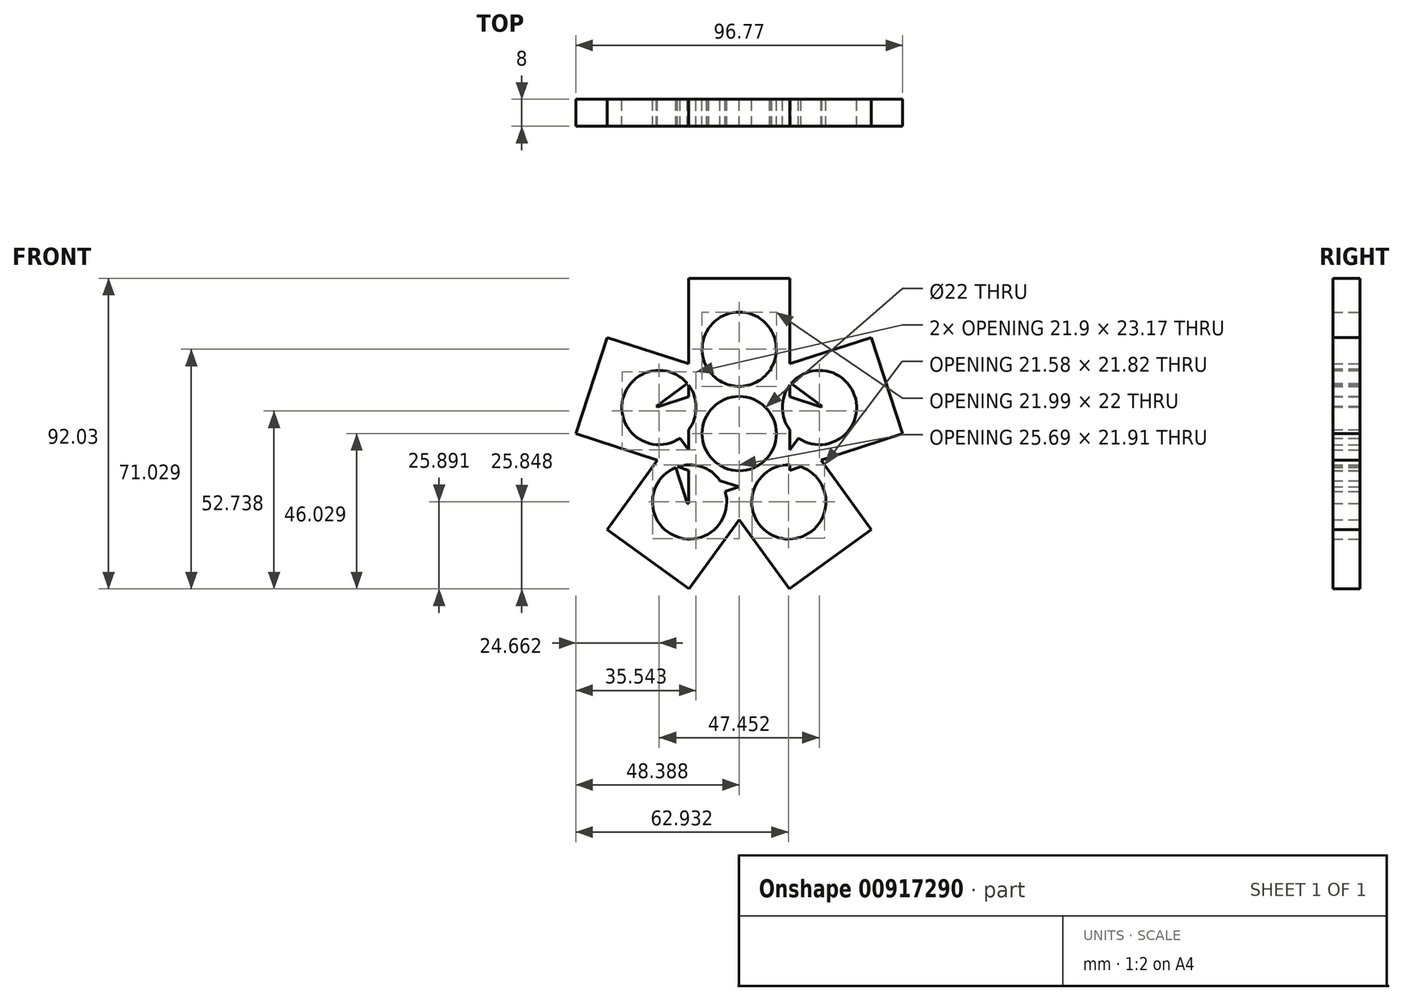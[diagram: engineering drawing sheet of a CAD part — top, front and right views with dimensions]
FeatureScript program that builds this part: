
annotation { "Feature Type Name" : "Feature", "Feature Type Description" : "" }
export const myFeature = defineFeature(function(context is Context, id is Id, definition is map)
    precondition{}
    {
        {
            var Q0;
            Q0=qCreatedBy(makeId("Front.planeOp"),FACE);
            var sketch = newSketch(context, id + "F0", { "sketchPlane" : qUnion([Q0])});
            skCircle(sketch, "E0", {"center": v(-106.85, -2.75) * mm, "radius": 11 * mm});
            skCircle(sketch, "E1", {"center": v(-106.85, -27.75) * mm, "radius": 11 * mm});
            skLineSegment(sketch, "E2.bottom", {"start": v(-121.85, 18.25) * mm, "end": v(-91.85, 18.25) * mm});
            skLineSegment(sketch, "E2.top", {"start": v(-121.85, -48.75) * mm, "end": v(-91.85, -48.75) * mm});
            skLineSegment(sketch, "E2.left", {"start": v(-121.85, 18.25) * mm, "end": v(-121.85, -48.75) * mm});
            skLineSegment(sketch, "E2.right", {"start": v(-91.85, 18.25) * mm, "end": v(-91.85, -48.75) * mm});
            skPoint(sketch, "E3", {"position": v(-106.85, 18.25) * mm});
            skLineSegment(sketch, "E4.1.0", {"start": v(-155.24, -27.8) * mm, "end": v(-91.52, -48.5) * mm});
            skLineSegment(sketch, "E4.1.1", {"start": v(-145.97, 0.73) * mm, "end": v(-82.24, -19.97) * mm});
            skCircle(sketch, "E4.1.2", {"center": v(-130.63, -20.03) * mm, "radius": 11 * mm});
            skLineSegment(sketch, "E4.1.3", {"start": v(-155.24, -27.8) * mm, "end": v(-145.97, 0.73) * mm});
            skLineSegment(sketch, "E4.1.5", {"start": v(-91.52, -48.5) * mm, "end": v(-82.24, -19.97) * mm});
            skPoint(sketch, "E4.1.6", {"position": v(-150.6, -13.54) * mm});
            skLineSegment(sketch, "E4.2.0", {"start": v(-121.76, -73.78) * mm, "end": v(-82.37, -19.58) * mm});
            skLineSegment(sketch, "E4.2.1", {"start": v(-146.03, -56.15) * mm, "end": v(-106.64, -1.94) * mm});
            skCircle(sketch, "E4.2.2", {"center": v(-121.55, -47.98) * mm, "radius": 11 * mm});
            skLineSegment(sketch, "E4.2.3", {"start": v(-121.76, -73.78) * mm, "end": v(-146.03, -56.15) * mm});
            skLineSegment(sketch, "E4.2.5", {"start": v(-82.37, -19.58) * mm, "end": v(-106.64, -1.94) * mm});
            skPoint(sketch, "E4.2.6", {"position": v(-133.9, -64.97) * mm});
            skLineSegment(sketch, "E5.2.3.0", {"start": v(-67.68, -56.15) * mm, "end": v(-107.06, -1.94) * mm});
            skLineSegment(sketch, "E5.3.3.0", {"start": v(-91.95, -73.78) * mm, "end": v(-131.33, -19.58) * mm});
            skCircle(sketch, "E5.6.3.0", {"center": v(-92.16, -47.98) * mm, "radius": 11 * mm});
            skLineSegment(sketch, "E5.8.3.0", {"start": v(-67.68, -56.15) * mm, "end": v(-91.95, -73.78) * mm});
            skLineSegment(sketch, "E5.13.3.0", {"start": v(-107.06, -1.94) * mm, "end": v(-131.33, -19.58) * mm});
            skPoint(sketch, "E5.16.3.0", {"position": v(-79.81, -64.97) * mm});
            skLineSegment(sketch, "E5.2.4.0", {"start": v(-67.74, 0.73) * mm, "end": v(-131.46, -19.97) * mm});
            skLineSegment(sketch, "E5.3.4.0", {"start": v(-58.47, -27.8) * mm, "end": v(-122.19, -48.5) * mm});
            skCircle(sketch, "E5.6.4.0", {"center": v(-83.08, -20.03) * mm, "radius": 11 * mm});
            skLineSegment(sketch, "E5.8.4.0", {"start": v(-67.74, 0.73) * mm, "end": v(-58.47, -27.8) * mm});
            skLineSegment(sketch, "E5.13.4.0", {"start": v(-131.46, -19.97) * mm, "end": v(-122.19, -48.5) * mm});
            skPoint(sketch, "E5.16.4.0", {"position": v(-63.1, -13.54) * mm});
            skSolve(sketch);
        }
        {
            var Q0;
            {var subQ5=sQuery(id+"F0.wireOp",EDGE,"E4.2.0");var subQ6=sQuery(id+"F0.wireOp",EDGE,"E2.right");var subQ7=makeQuery(id+"F0.imprint","INTERSECT",VERTEX,{"derivedFrom":[subQ6,subQ5]});Q0=makeQuery(id+"F0.imprint","IMPRINT",FACE,{"disambiguationData":[TD([[makeQuery(id+"F0.imprint","IMPRINT",EDGE,{"disambiguationData":[TD([[subQ7,-1.0]])],"derivedFrom":subQ6}),1.0]])]});}
            var Q1;
            {var subQ13=sQuery(id+"F0.wireOp",EDGE,"E5.8.4.0");Q1=makeQuery(id+"F0.imprint","IMPRINT",FACE,{"disambiguationData":[TD([[makeQuery(id+"F0.imprint","IMPRINT",EDGE,{"derivedFrom":subQ13}),-1.0]])]});}
            var Q2;
            {var subQ0=sQuery(id+"F0.wireOp",EDGE,"E5.2.3.0");var subQ9=sQuery(id+"F0.wireOp",EDGE,"E0");var subQ10=makeQuery(id+"F0.imprint","INTERSECT",VERTEX,{"derivedFrom":[subQ9,subQ0]});Q2=makeQuery(id+"F0.imprint","IMPRINT",FACE,{"disambiguationData":[TD([[makeQuery(id+"F0.imprint","IMPRINT",EDGE,{"disambiguationData":[TD([[subQ10,-1.0]])],"derivedFrom":subQ9}),-1.0]])]});}
            var Q3;
            {var subQ0=sQuery(id+"F0.wireOp",EDGE,"E5.3.3.0");var subQ6=sQuery(id+"F0.wireOp",EDGE,"E2.top");var subQ13=makeQuery(id+"F0.imprint","INTERSECT",VERTEX,{"derivedFrom":[subQ6,subQ0]});Q3=makeQuery(id+"F0.imprint","IMPRINT",FACE,{"disambiguationData":[TD([[makeQuery(id+"F0.imprint","IMPRINT",EDGE,{"disambiguationData":[TD([[subQ13,-1.0]])],"derivedFrom":subQ6}),1.0]])]});}
            var Q4;
            {var subQ0=sQuery(id+"F0.wireOp",EDGE,"E4.1.1");var subQ1=sQuery(id+"F0.wireOp",EDGE,"E2.left");var subQ2=makeQuery(id+"F0.imprint","INTERSECT",VERTEX,{"derivedFrom":[subQ1,subQ0]});Q4=makeQuery(id+"F0.imprint","IMPRINT",FACE,{"disambiguationData":[TD([[makeQuery(id+"F0.imprint","IMPRINT",EDGE,{"disambiguationData":[TD([[subQ2,-1.0]])],"derivedFrom":subQ1}),1.0]])]});}
            var Q5;
            {var subQ0=sQuery(id+"F0.wireOp",EDGE,"E5.3.3.0");var subQ1=sQuery(id+"F0.wireOp",EDGE,"E2.top");var subQ2=makeQuery(id+"F0.imprint","INTERSECT",VERTEX,{"derivedFrom":[subQ1,subQ0]});Q5=makeQuery(id+"F0.imprint","IMPRINT",FACE,{"disambiguationData":[TD([[makeQuery(id+"F0.imprint","IMPRINT",EDGE,{"disambiguationData":[TD([[subQ2,-1.0]])],"derivedFrom":subQ1}),-1.0]])]});}
            var Q6;
            {var subQ0=sQuery(id+"F0.wireOp",EDGE,"E5.8.3.0");Q6=makeQuery(id+"F0.imprint","IMPRINT",FACE,{"disambiguationData":[TD([[makeQuery(id+"F0.imprint","IMPRINT",EDGE,{"derivedFrom":subQ0}),-1.0]])]});}
            var Q7;
            {var subQ0=sQuery(id+"F0.wireOp",EDGE,"E4.2.3");Q7=makeQuery(id+"F0.imprint","IMPRINT",FACE,{"disambiguationData":[TD([[makeQuery(id+"F0.imprint","IMPRINT",EDGE,{"derivedFrom":subQ0}),-1.0]])]});}
            var Q8;
            {var subQ7=sQuery(id+"F0.wireOp",EDGE,"E4.1.1");var subQ8=sQuery(id+"F0.wireOp",EDGE,"E0");var subQ9=makeQuery(id+"F0.imprint","INTERSECT",VERTEX,{"disambiguationData":[OD(0.0)],"derivedFrom":[subQ8,subQ7]});Q8=makeQuery(id+"F0.imprint","IMPRINT",FACE,{"disambiguationData":[TD([[makeQuery(id+"F0.imprint","IMPRINT",EDGE,{"disambiguationData":[TD([[subQ9,-1.0]])],"derivedFrom":subQ8}),-1.0]])]});}
            var Q9;
            {var subQ1=sQuery(id+"F0.wireOp",EDGE,"E2.bottom");Q9=makeQuery(id+"F0.imprint","IMPRINT",FACE,{"disambiguationData":[TD([[makeQuery(id+"F0.imprint","IMPRINT",EDGE,{"derivedFrom":subQ1}),-1.0]])]});}
            var Q10;
            {var subQ0=sQuery(id+"F0.wireOp",EDGE,"E4.1.3");Q10=makeQuery(id+"F0.imprint","IMPRINT",FACE,{"disambiguationData":[TD([[makeQuery(id+"F0.imprint","IMPRINT",EDGE,{"derivedFrom":subQ0}),-1.0]])]});}
            var Q11;
            {var subQ0=sQuery(id+"F0.wireOp",EDGE,"E5.2.4.0");var subQ1=sQuery(id+"F0.wireOp",EDGE,"E2.right");var subQ2=makeQuery(id+"F0.imprint","INTERSECT",VERTEX,{"derivedFrom":[subQ1,subQ0]});Q11=makeQuery(id+"F0.imprint","IMPRINT",FACE,{"disambiguationData":[TD([[makeQuery(id+"F0.imprint","IMPRINT",EDGE,{"disambiguationData":[TD([[subQ2,-1.0]])],"derivedFrom":subQ1}),-1.0]])]});}
            var Q12;
            {var subQ0=sQuery(id+"F0.wireOp",EDGE,"E4.2.1");var subQ1=sQuery(id+"F0.wireOp",EDGE,"E0");var subQ2=makeQuery(id+"F0.imprint","INTERSECT",VERTEX,{"derivedFrom":[subQ1,subQ0]});Q12=makeQuery(id+"F0.imprint","IMPRINT",FACE,{"disambiguationData":[TD([[makeQuery(id+"F0.imprint","IMPRINT",EDGE,{"disambiguationData":[TD([[subQ2,-1.0]])],"derivedFrom":subQ1}),-1.0]])]});}
            var Q13;
            {var subQ0=sQuery(id+"F0.wireOp",EDGE,"E5.2.4.0");var subQ1=sQuery(id+"F0.wireOp",EDGE,"E0");var subQ2=makeQuery(id+"F0.imprint","INTERSECT",VERTEX,{"disambiguationData":[OD(1.0)],"derivedFrom":[subQ1,subQ0]});Q13=makeQuery(id+"F0.imprint","IMPRINT",FACE,{"disambiguationData":[TD([[makeQuery(id+"F0.imprint","IMPRINT",EDGE,{"disambiguationData":[TD([[subQ2,-1.0]])],"derivedFrom":subQ1}),-1.0]])]});}
            var Q14;
            {var subQ0=sQuery(id+"F0.wireOp",EDGE,"E5.3.4.0");var subQ1=sQuery(id+"F0.wireOp",EDGE,"E4.1.0");var subQ2=makeQuery(id+"F0.imprint","INTERSECT",VERTEX,{"derivedFrom":[subQ1,subQ0]});Q14=makeQuery(id+"F0.imprint","IMPRINT",FACE,{"disambiguationData":[TD([[makeQuery(id+"F0.imprint","IMPRINT",EDGE,{"disambiguationData":[TD([[subQ2,-1.0]])],"derivedFrom":subQ1}),1.0]])]});}
            var Q15;
            {var subQ0=sQuery(id+"F0.wireOp",EDGE,"E4.1.1");var subQ1=sQuery(id+"F0.wireOp",EDGE,"E0");var subQ2=makeQuery(id+"F0.imprint","INTERSECT",VERTEX,{"disambiguationData":[OD(0.0)],"derivedFrom":[subQ1,subQ0]});Q15=makeQuery(id+"F0.imprint","IMPRINT",FACE,{"disambiguationData":[TD([[makeQuery(id+"F0.imprint","IMPRINT",EDGE,{"disambiguationData":[TD([[subQ2,1.0]])],"derivedFrom":subQ1}),-1.0]])]});}
            var Q16;
            {var subQ0=sQuery(id+"F0.wireOp",EDGE,"E4.2.1");var subQ1=sQuery(id+"F0.wireOp",EDGE,"E4.1.2");var subQ2=makeQuery(id+"F0.imprint","INTERSECT",VERTEX,{"disambiguationData":[OD(0.0)],"derivedFrom":[subQ1,subQ0]});Q16=makeQuery(id+"F0.imprint","IMPRINT",FACE,{"disambiguationData":[TD([[makeQuery(id+"F0.imprint","IMPRINT",EDGE,{"disambiguationData":[TD([[subQ2,1.0]])],"derivedFrom":subQ1}),-1.0]])]});}
            var Q17;
            {var subQ0=sQuery(id+"F0.wireOp",EDGE,"E4.1.1");var subQ1=sQuery(id+"F0.wireOp",EDGE,"E0");var subQ2=makeQuery(id+"F0.imprint","INTERSECT",VERTEX,{"disambiguationData":[OD(1.0)],"derivedFrom":[subQ1,subQ0]});Q17=makeQuery(id+"F0.imprint","IMPRINT",FACE,{"disambiguationData":[TD([[makeQuery(id+"F0.imprint","IMPRINT",EDGE,{"disambiguationData":[TD([[subQ2,-1.0]])],"derivedFrom":subQ1}),-1.0]])]});}
            var Q18;
            {var subQ0=sQuery(id+"F0.wireOp",EDGE,"E4.2.2");var subQ1=sQuery(id+"F0.wireOp",EDGE,"E4.1.0");var subQ2=makeQuery(id+"F0.imprint","INTERSECT",VERTEX,{"disambiguationData":[OD(1.0)],"derivedFrom":[subQ1,subQ0]});Q18=makeQuery(id+"F0.imprint","IMPRINT",FACE,{"disambiguationData":[TD([[makeQuery(id+"F0.imprint","IMPRINT",EDGE,{"disambiguationData":[TD([[subQ2,-1.0]])],"derivedFrom":subQ1}),-1.0]])]});}
            var Q19;
            {var subQ0=sQuery(id+"F0.wireOp",EDGE,"E5.2.3.0");var subQ1=sQuery(id+"F0.wireOp",EDGE,"E4.1.1");var subQ2=makeQuery(id+"F0.imprint","INTERSECT",VERTEX,{"derivedFrom":[subQ1,subQ0]});Q19=makeQuery(id+"F0.imprint","IMPRINT",FACE,{"disambiguationData":[TD([[makeQuery(id+"F0.imprint","IMPRINT",EDGE,{"disambiguationData":[TD([[subQ2,-1.0]])],"derivedFrom":subQ1}),-1.0]])]});}
            var Q20;
            {var subQ0=sQuery(id+"F0.wireOp",EDGE,"E4.2.1");var subQ1=sQuery(id+"F0.wireOp",EDGE,"E4.1.0");var subQ2=makeQuery(id+"F0.imprint","INTERSECT",VERTEX,{"derivedFrom":[subQ1,subQ0]});Q20=makeQuery(id+"F0.imprint","IMPRINT",FACE,{"disambiguationData":[TD([[makeQuery(id+"F0.imprint","IMPRINT",EDGE,{"disambiguationData":[TD([[subQ2,-1.0]])],"derivedFrom":subQ1}),1.0]])]});}
            var Q21;
            {var subQ0=sQuery(id+"F0.wireOp",EDGE,"E5.6.3.0");var subQ1=sQuery(id+"F0.wireOp",EDGE,"E2.right");var subQ2=makeQuery(id+"F0.imprint","INTERSECT",VERTEX,{"derivedFrom":[subQ1,subQ0]});Q21=makeQuery(id+"F0.imprint","IMPRINT",FACE,{"disambiguationData":[TD([[makeQuery(id+"F0.imprint","IMPRINT",EDGE,{"disambiguationData":[TD([[subQ2,-1.0]])],"derivedFrom":subQ1}),1.0]])]});}
            var Q22;
            {var subQ0=sQuery(id+"F0.wireOp",EDGE,"E4.2.0");var subQ1=sQuery(id+"F0.wireOp",EDGE,"E2.right");var subQ2=makeQuery(id+"F0.imprint","INTERSECT",VERTEX,{"derivedFrom":[subQ1,subQ0]});Q22=makeQuery(id+"F0.imprint","IMPRINT",FACE,{"disambiguationData":[TD([[makeQuery(id+"F0.imprint","IMPRINT",EDGE,{"disambiguationData":[TD([[subQ2,-1.0]])],"derivedFrom":subQ1}),-1.0]])]});}
            var Q23;
            {var subQ0=sQuery(id+"F0.wireOp",EDGE,"E5.6.4.0");var subQ1=sQuery(id+"F0.wireOp",EDGE,"E2.right");var subQ2=makeQuery(id+"F0.imprint","INTERSECT",VERTEX,{"disambiguationData":[OD(1.0)],"derivedFrom":[subQ1,subQ0]});Q23=makeQuery(id+"F0.imprint","IMPRINT",FACE,{"disambiguationData":[TD([[makeQuery(id+"F0.imprint","IMPRINT",EDGE,{"disambiguationData":[TD([[subQ2,-1.0]])],"derivedFrom":subQ1}),1.0]])]});}
            var Q24;
            {var subQ0=sQuery(id+"F0.wireOp",EDGE,"E4.1.2");var subQ1=sQuery(id+"F0.wireOp",EDGE,"E2.left");var subQ2=makeQuery(id+"F0.imprint","INTERSECT",VERTEX,{"disambiguationData":[OD(1.0)],"derivedFrom":[subQ1,subQ0]});Q24=makeQuery(id+"F0.imprint","IMPRINT",FACE,{"disambiguationData":[TD([[makeQuery(id+"F0.imprint","IMPRINT",EDGE,{"disambiguationData":[TD([[subQ2,-1.0]])],"derivedFrom":subQ1}),-1.0]])]});}
            var Q25;
            {var subQ0=sQuery(id+"F0.wireOp",EDGE,"E5.3.3.0");var subQ1=sQuery(id+"F0.wireOp",EDGE,"E2.left");var subQ2=makeQuery(id+"F0.imprint","INTERSECT",VERTEX,{"derivedFrom":[subQ1,subQ0]});Q25=makeQuery(id+"F0.imprint","IMPRINT",FACE,{"disambiguationData":[TD([[makeQuery(id+"F0.imprint","IMPRINT",EDGE,{"disambiguationData":[TD([[subQ2,-1.0]])],"derivedFrom":subQ1}),1.0]])]});}
            var Q26;
            {var subQ0=sQuery(id+"F0.wireOp",EDGE,"E4.2.5");var subQ1=sQuery(id+"F0.wireOp",EDGE,"E2.right");var subQ2=makeQuery(id+"F0.imprint","INTERSECT",VERTEX,{"derivedFrom":[subQ1,subQ0]});Q26=makeQuery(id+"F0.imprint","IMPRINT",FACE,{"disambiguationData":[TD([[makeQuery(id+"F0.imprint","IMPRINT",EDGE,{"disambiguationData":[TD([[subQ2,-1.0]])],"derivedFrom":subQ1}),1.0]])]});}
            var Q27;
            {var subQ0=sQuery(id+"F0.wireOp",EDGE,"E5.6.4.0");var subQ1=sQuery(id+"F0.wireOp",EDGE,"E2.right");var subQ2=makeQuery(id+"F0.imprint","INTERSECT",VERTEX,{"disambiguationData":[OD(0.0)],"derivedFrom":[subQ1,subQ0]});Q27=makeQuery(id+"F0.imprint","IMPRINT",FACE,{"disambiguationData":[TD([[makeQuery(id+"F0.imprint","IMPRINT",EDGE,{"disambiguationData":[TD([[subQ2,-1.0]])],"derivedFrom":subQ1}),-1.0]])]});}
            var Q28;
            {var subQ0=sQuery(id+"F0.wireOp",EDGE,"E4.2.1");var subQ1=sQuery(id+"F0.wireOp",EDGE,"E4.1.2");var subQ2=makeQuery(id+"F0.imprint","INTERSECT",VERTEX,{"disambiguationData":[OD(1.0)],"derivedFrom":[subQ1,subQ0]});Q28=makeQuery(id+"F0.imprint","IMPRINT",FACE,{"disambiguationData":[TD([[makeQuery(id+"F0.imprint","IMPRINT",EDGE,{"disambiguationData":[TD([[subQ2,-1.0]])],"derivedFrom":subQ1}),-1.0]])]});}
            var Q29;
            {var subQ0=sQuery(id+"F0.wireOp",EDGE,"E5.3.4.0");var subQ1=sQuery(id+"F0.wireOp",EDGE,"E4.1.5");var subQ2=makeQuery(id+"F0.imprint","INTERSECT",VERTEX,{"derivedFrom":[subQ1,subQ0]});Q29=makeQuery(id+"F0.imprint","IMPRINT",FACE,{"disambiguationData":[TD([[makeQuery(id+"F0.imprint","IMPRINT",EDGE,{"disambiguationData":[TD([[subQ2,-1.0]])],"derivedFrom":subQ1}),-1.0]])]});}
            var Q30;
            {var subQ0=sQuery(id+"F0.wireOp",EDGE,"E5.2.3.0");var subQ1=sQuery(id+"F0.wireOp",EDGE,"E4.1.5");var subQ2=makeQuery(id+"F0.imprint","INTERSECT",VERTEX,{"derivedFrom":[subQ1,subQ0]});Q30=makeQuery(id+"F0.imprint","IMPRINT",FACE,{"disambiguationData":[TD([[makeQuery(id+"F0.imprint","IMPRINT",EDGE,{"disambiguationData":[TD([[subQ2,-1.0]])],"derivedFrom":subQ1}),1.0]])]});}
            var Q31;
            {var subQ0=sQuery(id+"F0.wireOp",EDGE,"E4.2.2");var subQ1=sQuery(id+"F0.wireOp",EDGE,"E2.top");var subQ2=makeQuery(id+"F0.imprint","INTERSECT",VERTEX,{"derivedFrom":[subQ1,subQ0]});Q31=makeQuery(id+"F0.imprint","IMPRINT",FACE,{"disambiguationData":[TD([[makeQuery(id+"F0.imprint","IMPRINT",EDGE,{"disambiguationData":[TD([[subQ2,-1.0]])],"derivedFrom":subQ1}),1.0]])]});}
            var Q32;
            {var subQ0=sQuery(id+"F0.wireOp",EDGE,"E4.2.0");var subQ1=sQuery(id+"F0.wireOp",EDGE,"E2.top");var subQ2=makeQuery(id+"F0.imprint","INTERSECT",VERTEX,{"derivedFrom":[subQ1,subQ0]});Q32=makeQuery(id+"F0.imprint","IMPRINT",FACE,{"disambiguationData":[TD([[makeQuery(id+"F0.imprint","IMPRINT",EDGE,{"disambiguationData":[TD([[subQ2,-1.0]])],"derivedFrom":subQ1}),1.0]])]});}
            var Q33;
            {var subQ0=sQuery(id+"F0.wireOp",EDGE,"E5.13.4.0");var subQ1=sQuery(id+"F0.wireOp",EDGE,"E4.1.0");var subQ2=makeQuery(id+"F0.imprint","INTERSECT",VERTEX,{"derivedFrom":[subQ1,subQ0]});Q33=makeQuery(id+"F0.imprint","IMPRINT",FACE,{"disambiguationData":[TD([[makeQuery(id+"F0.imprint","IMPRINT",EDGE,{"disambiguationData":[TD([[subQ2,-1.0]])],"derivedFrom":subQ1}),-1.0]])]});}
            var Q34;
            {var subQ0=sQuery(id+"F0.wireOp",EDGE,"E5.13.3.0");var subQ1=sQuery(id+"F0.wireOp",EDGE,"E2.left");var subQ2=makeQuery(id+"F0.imprint","INTERSECT",VERTEX,{"derivedFrom":[subQ1,subQ0]});Q34=makeQuery(id+"F0.imprint","IMPRINT",FACE,{"disambiguationData":[TD([[makeQuery(id+"F0.imprint","IMPRINT",EDGE,{"disambiguationData":[TD([[subQ2,-1.0]])],"derivedFrom":subQ1}),-1.0]])]});}
            var Q35;
            {var subQ0=sQuery(id+"F0.wireOp",EDGE,"E5.6.3.0");var subQ1=sQuery(id+"F0.wireOp",EDGE,"E4.1.5");var subQ2=makeQuery(id+"F0.imprint","INTERSECT",VERTEX,{"derivedFrom":[subQ1,subQ0]});Q35=makeQuery(id+"F0.imprint","IMPRINT",FACE,{"disambiguationData":[TD([[makeQuery(id+"F0.imprint","IMPRINT",EDGE,{"disambiguationData":[TD([[subQ2,-1.0]])],"derivedFrom":subQ1}),1.0]])]});}
            var Q36;
            Q36=makeQuery(id+"F0.imprint","IMPRINT",FACE,{"disambiguationData":[TD([[makeQuery(id+"F0.imprint","IMPRINT",EDGE,{"derivedFrom":sQuery(id+"F0.wireOp",EDGE,"E1")}),-1.0]])]});
            var Q37;
            {var subQ5=sQuery(id+"F0.wireOp",EDGE,"E5.3.3.0");var subQ11=sQuery(id+"F0.wireOp",EDGE,"E2.left");var subQ12=makeQuery(id+"F0.imprint","INTERSECT",VERTEX,{"derivedFrom":[subQ11,subQ5]});Q37=makeQuery(id+"F0.imprint","IMPRINT",FACE,{"disambiguationData":[TD([[makeQuery(id+"F0.imprint","IMPRINT",EDGE,{"disambiguationData":[TD([[subQ12,-1.0]])],"derivedFrom":subQ11}),-1.0]])]});}
            extrude(context, id + "F1", {"entities" : qUnion([Q0, Q1, Q2, Q3, Q4, Q5, Q6, Q7, Q8, Q9, Q10, Q11, Q12, Q13, Q14, Q15, Q16, Q17, Q18, Q19, Q20, Q21, Q22, Q23, Q24, Q25, Q26, Q27, Q28, Q29, Q30, Q31, Q32, Q33, Q34, Q35, Q36, Q37]), "depth" : 8 * mm, "offsetDistance" : 25 * mm});
        }
    });
